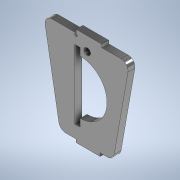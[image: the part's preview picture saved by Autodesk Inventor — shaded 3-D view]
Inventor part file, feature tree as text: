
AUTODESK INVENTOR PART (.ipt)
format: ipt  version: 2021 (Build 250183000, 183)  size: 181,248 bytes
history: native  units: in
note: dims shown in document units (in); Inventor stores cm internally (conversion verified against a paired STEP export)
features: extrude x8, sketch x4
ambient origin geometry x8: Origin, YZ Plane, XZ Plane, XY Plane, X Axis, Y Axis, Z Axis, Center Point
bodies: Solid1 (feature_tree)
feature tree (12):
  sketch  "Sketch1"  dims[d1=0.0787in d2=0.6871in]
  extrude  "Extrusion1"  Depth=0.0787in
  extrude  "Extrusion2"  Depth=0.0039in
  extrude  "Extrusion3"  Depth=0.0787in
  extrude  "Extrusion6"  Depth=0.1772in
  extrude  "Extrusion7"  Depth=0.3937in
  extrude  "Extrusão8"  Depth=0.3937in
  extrude  "Extrusão9"  Depth=0.0354in
  extrude  "Extrusão10"  Depth=0.0354in
  sketch  "Esboço2"  dims[d3=0.9843in d4=0.0039in]
  sketch  "Esboço3"  dims[d5=0.0787in d6=0.1181in]
  sketch  "Esboço4"  dims[d7=0.1772in d8=0.1772in d9=0.6871in d10=0.9843in d11=0.0354in d12=0.0354in d13=0.0787in d16=0.3937in d17=0.3937in d18=0.0787in d19=0.0in d20=0.0394in d21=0.0in d22=0.0394in d23=0.0in d28=0.0394in d29=0.0in d30=0.0394in d31=0.0in d32=0.0787in d33=0.0in d34=0.0591in d35=0.0in d36=0.7874in d37=0.0591in d38=0.3937in d39=0.3937in d40=0.0in]
